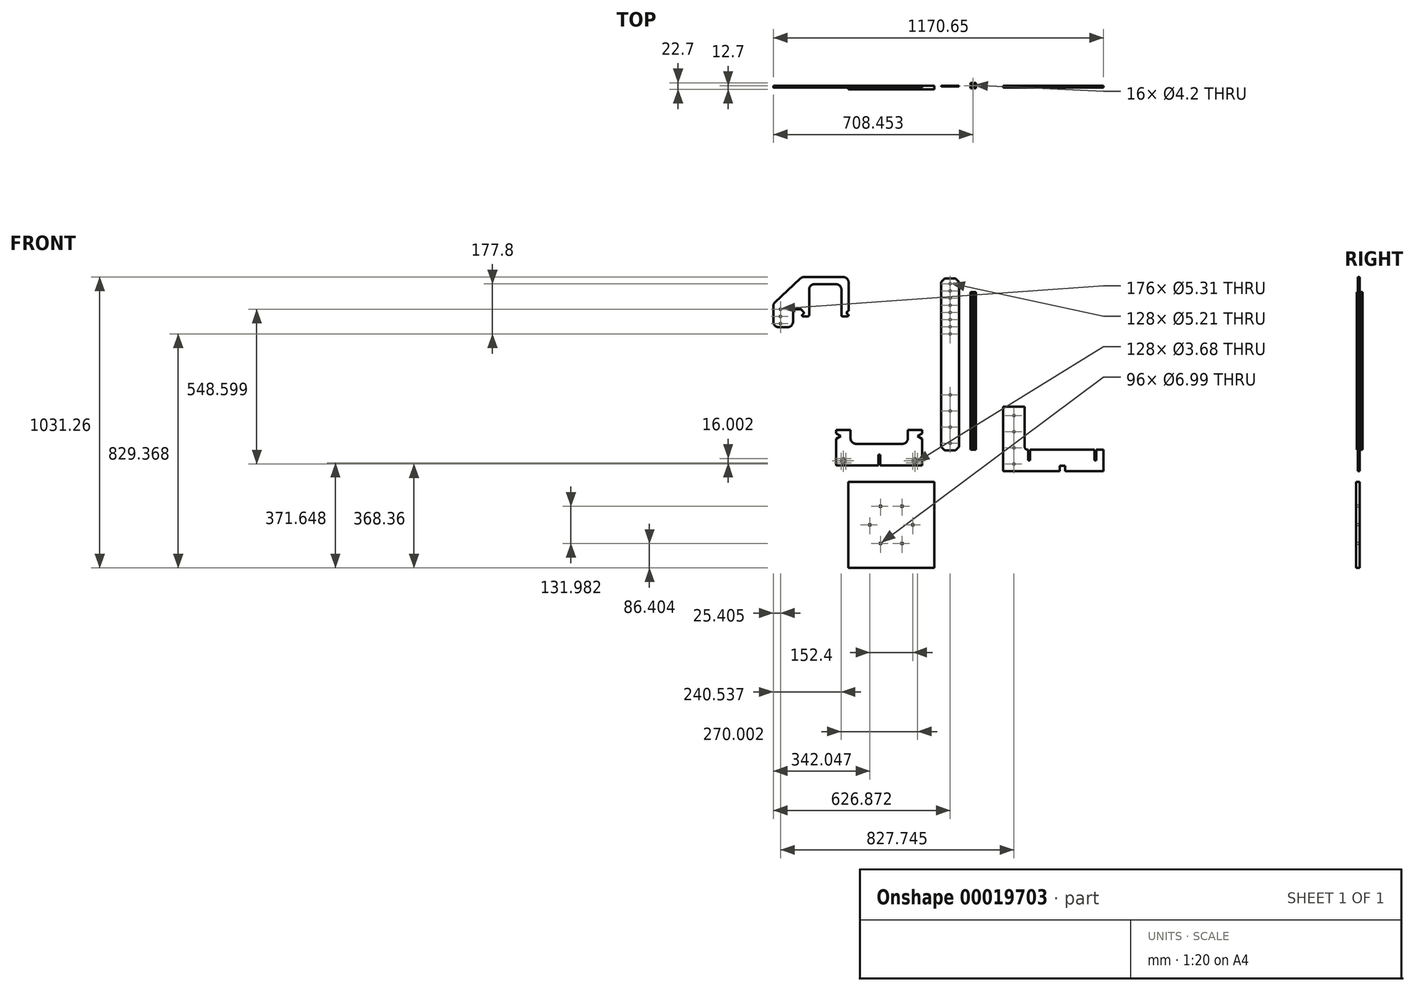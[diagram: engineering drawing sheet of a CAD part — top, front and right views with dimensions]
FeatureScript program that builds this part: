
annotation { "Feature Type Name" : "Feature", "Feature Type Description" : "" }
export const myFeature = defineFeature(function(context is Context, id is Id, definition is map)
    precondition{}
    {
        {
            var Q0;
            Q0=qCreatedBy(makeId("Front.planeOp"),FACE);
            var sketch = newSketch(context, id + "F0", { "sketchPlane" : qUnion([Q0])});
            skLineSegment(sketch, "E0.bottom", {"start": v(76.2, 0) * mm, "end": v(88.9, 0) * mm});
            skLineSegment(sketch, "E0.top", {"start": v(0, -76.2) * mm, "end": v(355.6, -76.2) * mm});
            skLineSegment(sketch, "E0.left", {"start": v(0, 0) * mm, "end": v(0, -76.2) * mm});
            skLineSegment(sketch, "E0.right", {"start": v(355.6, 0) * mm, "end": v(355.6, -76.2) * mm});
            skLineSegment(sketch, "E1.top", {"start": v(0, 152.4) * mm, "end": v(76.2, 152.4) * mm});
            skLineSegment(sketch, "E1.left", {"start": v(0, 0) * mm, "end": v(0, 152.4) * mm});
            skLineSegment(sketch, "E1.right", {"start": v(76.2, 0) * mm, "end": v(76.2, 152.4) * mm});
            skLineSegment(sketch, "E2.top", {"start": v(88.9, -38.1) * mm, "end": v(95.25, -38.1) * mm});
            skLineSegment(sketch, "E2.left", {"start": v(88.9, 0) * mm, "end": v(88.9, -38.1) * mm});
            skLineSegment(sketch, "E2.right", {"start": v(95.25, 0) * mm, "end": v(95.25, -38.1) * mm});
            skLineSegment(sketch, "E3.top", {"start": v(323.85, -38.1) * mm, "end": v(330.2, -38.1) * mm});
            skLineSegment(sketch, "E3.left", {"start": v(323.85, 0) * mm, "end": v(323.85, -38.1) * mm});
            skLineSegment(sketch, "E3.right", {"start": v(330.2, 0) * mm, "end": v(330.2, -38.1) * mm});
            skLineSegment(sketch, "E4.trimOffspring", {"start": v(95.25, 0) * mm, "end": v(323.85, 0) * mm});
            skLineSegment(sketch, "E5.trimOffspring", {"start": v(330.2, 0) * mm, "end": v(355.6, 0) * mm});
            skSolve(sketch);
        }
        {
            var Q0;
            Q0 = qSketchRegion(id + "F0", true);
            extrude(context, id + "F1", {"entities" : qUnion([Q0]), "depth" : 6.35 * mm});
        }
        {
            var Q0;
            Q0=qCreatedBy(makeId("Front.planeOp"),FACE);
            var sketch = newSketch(context, id + "F2", { "sketchPlane" : qUnion([Q0])});
            skLineSegment(sketch, "E6.bottom", {"start": v(-541.11, 20.69) * mm, "end": v(-337.91, 20.69) * mm});
            skLineSegment(sketch, "E6.top", {"start": v(-591.91, -55.51) * mm, "end": v(-442.69, -55.51) * mm});
            skLineSegment(sketch, "E6.left", {"start": v(-591.91, 20.69) * mm, "end": v(-591.91, -55.51) * mm});
            skLineSegment(sketch, "E6.right", {"start": v(-287.11, 20.69) * mm, "end": v(-287.11, -55.51) * mm});
            skLineSegment(sketch, "E7.top", {"start": v(-591.91, 70.22) * mm, "end": v(-541.11, 70.22) * mm});
            skLineSegment(sketch, "E7.left", {"start": v(-591.91, 20.69) * mm, "end": v(-591.91, 38.47) * mm});
            skLineSegment(sketch, "E7.right", {"start": v(-541.11, 20.69) * mm, "end": v(-541.11, 70.22) * mm});
            skLineSegment(sketch, "E8.top", {"start": v(-287.11, 70.22) * mm, "end": v(-337.91, 70.22) * mm});
            skLineSegment(sketch, "E8.left", {"start": v(-287.11, 20.69) * mm, "end": v(-287.11, 38.47) * mm});
            skLineSegment(sketch, "E8.right", {"start": v(-337.91, 20.69) * mm, "end": v(-337.91, 70.22) * mm});
            skLineSegment(sketch, "E9.top", {"start": v(-442.69, -17.41) * mm, "end": v(-436.34, -17.41) * mm});
            skLineSegment(sketch, "E9.left", {"start": v(-442.69, -55.51) * mm, "end": v(-442.69, -17.41) * mm});
            skLineSegment(sketch, "E9.right", {"start": v(-436.34, -55.51) * mm, "end": v(-436.34, -17.41) * mm});
            skLineSegment(sketch, "E10.trimOffspring", {"start": v(-318.86, -55.51) * mm, "end": v(-287.11, -55.51) * mm});
            skLineSegment(sketch, "E11.trimOffspring", {"start": v(-436.34, -55.51) * mm, "end": v(-325.21, -55.51) * mm});
            skLineSegment(sketch, "E12", {"start": v(-325.21, -55.51) * mm, "end": v(-318.86, -55.51) * mm});
            skLineSegment(sketch, "E13", {"start": v(-591.91, 57.52) * mm, "end": v(-575.41, 48) * mm});
            skLineSegment(sketch, "E14", {"start": v(-575.41, 48) * mm, "end": v(-591.91, 38.47) * mm});
            skLineSegment(sketch, "E15", {"start": v(-439.51, 20.69) * mm, "end": v(-439.51, -17.41) * mm, "construction": true});
            skLineSegment(sketch, "E16.MirrorCS", {"start": v(-287.11, 57.52) * mm, "end": v(-303.6, 48) * mm});
            skLineSegment(sketch, "E17.MirrorCS", {"start": v(-303.6, 48) * mm, "end": v(-287.11, 38.47) * mm});
            skLineSegment(sketch, "E18.trimOffspring", {"start": v(-591.91, 57.52) * mm, "end": v(-591.91, 70.22) * mm});
            skLineSegment(sketch, "E19.trimOffspring", {"start": v(-287.11, 57.52) * mm, "end": v(-287.11, 70.22) * mm});
            skSolve(sketch);
        }
        {
            var Q0;
            Q0 = qSketchRegion(id + "F2", true);
            extrude(context, id + "F3", {"entities" : qUnion([Q0]), "depth" : 6.35 * mm});
        }
        {
            var Q0;
            Q0=qCreatedBy(makeId("Front.planeOp"),FACE);
            var sketch = newSketch(context, id + "F4", { "sketchPlane" : qUnion([Q0])});
            skLineSegment(sketch, "E20.bottom", {"start": v(-815.05, 516.85) * mm, "end": v(-750.47, 516.85) * mm, "construction": true});
            skLineSegment(sketch, "E21.bottom", {"start": v(-713.45, 472.4) * mm, "end": v(-688.05, 472.4) * mm});
            skLineSegment(sketch, "E21.top", {"start": v(-713.45, 612.1) * mm, "end": v(-548.35, 612.1) * mm});
            skLineSegment(sketch, "E22.top", {"start": v(-688.05, 586.7) * mm, "end": v(-573.75, 586.7) * mm});
            skLineSegment(sketch, "E22.left", {"start": v(-688.05, 472.4) * mm, "end": v(-688.05, 586.7) * mm});
            skLineSegment(sketch, "E22.right", {"start": v(-573.75, 472.4) * mm, "end": v(-573.75, 586.7) * mm});
            skLineSegment(sketch, "E23.trimOffspring", {"start": v(-573.75, 472.4) * mm, "end": v(-548.35, 472.4) * mm});
            skArc(sketch, "E24", {"start": v(-713.45, 478.75) * mm, "mid": v(-707.1, 485.1) * mm, "end": v(-713.45, 491.45) * mm});
            skLineSegment(sketch, "E25.trimOffspring", {"start": v(-548.35, 574) * mm, "end": v(-548.35, 612.1) * mm});
            skLineSegment(sketch, "E26", {"start": v(-815.05, 516.85) * mm, "end": v(-815.05, 497.8) * mm});
            skCircle(sketch, "E27", {"center": v(-789.65, 497.8) * mm, "radius": 2.65 * mm});
            skCircle(sketch, "E28.0.1.0", {"center": v(-789.65, 472.4) * mm, "radius": 2.65 * mm});
            skCircle(sketch, "E28.0.2.0", {"center": v(-789.65, 447) * mm, "radius": 2.65 * mm});
            skLineSegment(sketch, "E29", {"start": v(-548.35, 574) * mm, "end": v(-548.35, 491.45) * mm});
            skLineSegment(sketch, "E30", {"start": v(-745.2, 497.8) * mm, "end": v(-713.45, 497.8) * mm});
            skLineSegment(sketch, "E31", {"start": v(-713.45, 497.8) * mm, "end": v(-713.45, 491.45) * mm});
            skPoint(sketch, "E32.orphan", {"position": v(-745.2, 472.4) * mm});
            skLineSegment(sketch, "E33", {"start": v(-750.47, 516.85) * mm, "end": v(-713.45, 516.85) * mm, "construction": true});
            skLineSegment(sketch, "E34", {"start": v(-713.45, 516.85) * mm, "end": v(-713.45, 612.1) * mm, "construction": true});
            skPoint(sketch, "E35.trimOffspring.end.orphan", {"position": v(-734.5, 612.1) * mm});
            skArc(sketch, "E36.1.0.0", {"start": v(-548.35, 491.45) * mm, "mid": v(-554.7, 485.1) * mm, "end": v(-548.35, 478.75) * mm});
            skLineSegment(sketch, "E36.direction1", {"start": v(-713.45, 485.1) * mm, "end": v(-548.35, 485.1) * mm, "construction": true});
            skLineSegment(sketch, "E37.trimOffspring", {"start": v(-713.45, 478.75) * mm, "end": v(-713.45, 472.4) * mm});
            skLineSegment(sketch, "E38.trimOffspring", {"start": v(-548.35, 478.75) * mm, "end": v(-548.35, 472.4) * mm});
            skLineSegment(sketch, "E39", {"start": v(-745.2, 497.8) * mm, "end": v(-745.2, 434.3) * mm});
            skLineSegment(sketch, "E40", {"start": v(-745.2, 434.3) * mm, "end": v(-815.05, 434.3) * mm});
            skLineSegment(sketch, "E41", {"start": v(-815.05, 434.3) * mm, "end": v(-815.05, 497.8) * mm});
            skLineSegment(sketch, "E42", {"start": v(-815.05, 516.85) * mm, "end": v(-713.45, 612.1) * mm});
            skSolve(sketch);
        }
        {
            var Q0;
            Q0 = qSketchRegion(id + "F4", true);
            extrude(context, id + "F5", {"entities" : qUnion([Q0]), "depth" : 6.35 * mm});
        }
        {
            var Q0;
            Q0=qCreatedBy(makeId("Front.planeOp"),FACE);
            var sketch = newSketch(context, id + "F6", { "sketchPlane" : qUnion([Q0])});
            skLineSegment(sketch, "E43.bottom", {"start": v(-549.2, -114.36) * mm, "end": v(-244.4, -114.36) * mm});
            skLineSegment(sketch, "E43.top", {"start": v(-549.2, -419.16) * mm, "end": v(-244.4, -419.16) * mm});
            skLineSegment(sketch, "E43.left", {"start": v(-549.2, -114.36) * mm, "end": v(-549.2, -419.16) * mm});
            skLineSegment(sketch, "E43.right", {"start": v(-244.4, -114.36) * mm, "end": v(-244.4, -419.16) * mm});
            skSolve(sketch);
        }
        {
            var Q0;
            Q0 = qSketchRegion(id + "F6", true);
            extrude(context, id + "F7", {"entities" : qUnion([Q0]), "depth" : 12.7 * mm});
        }
        {
            var Q0;
            Q0=makeQuery(id+"F1.opExtrude","CAP_FACE",FACE,{"disambiguationData":[OSD([sQuery(id+"F0.wireOp",EDGE,"E0.bottom"),sQuery(id+"F0.wireOp",EDGE,"E0.top"),sQuery(id+"F0.wireOp",EDGE,"E0.left"),sQuery(id+"F0.wireOp",EDGE,"E0.right"),sQuery(id+"F0.wireOp",EDGE,"E1.top"),sQuery(id+"F0.wireOp",EDGE,"E1.left"),sQuery(id+"F0.wireOp",EDGE,"E1.right"),sQuery(id+"F0.wireOp",EDGE,"a85b3c0d-053f-45aa-b62b-9afe83705e7b.bottom"),sQuery(id+"F0.wireOp",EDGE,"a85b3c0d-053f-45aa-b62b-9afe83705e7b.top"),sQuery(id+"F0.wireOp",EDGE,"a85b3c0d-053f-45aa-b62b-9afe83705e7b.right"),sQuery(id+"F0.wireOp",EDGE,"E2.top"),sQuery(id+"F0.wireOp",EDGE,"E2.left"),sQuery(id+"F0.wireOp",EDGE,"E2.right"),sQuery(id+"F0.wireOp",EDGE,"E3.top"),sQuery(id+"F0.wireOp",EDGE,"E3.left"),sQuery(id+"F0.wireOp",EDGE,"E3.right"),sQuery(id+"F0.wireOp",EDGE,"2a624cb3-e000-4eb9-9106-63d80287ee97.trimOffspring"),sQuery(id+"F0.wireOp",EDGE,"E4.trimOffspring"),sQuery(id+"F0.wireOp",EDGE,"E5.trimOffspring")])],"isStart":false});
            var sketch = newSketch(context, id + "F8", { "sketchPlane" : qUnion([Q0])});
            skCircle(sketch, "E44", {"center": v(38.1, -50.8) * mm, "radius": 2.65 * mm});
            skCircle(sketch, "E45.0.1.0", {"center": v(38.1, 6.35) * mm, "radius": 2.65 * mm});
            skCircle(sketch, "E45.0.2.0", {"center": v(38.1, 63.5) * mm, "radius": 2.65 * mm});
            skCircle(sketch, "E46", {"center": v(38.1, 120.65) * mm, "radius": 2.65 * mm});
            skSolve(sketch);
        }
        {
            var Q0;
            Q0 = qSketchRegion(id + "F8", true);
            extrude(context, id + "F9", {"entities" : qUnion([Q0]), "operationType" : NewBodyOperationType.REMOVE, "endBound" : BoundingType.SYMMETRIC, "oppositeDirection" : true, "depth" : 25.4 * mm});
        }
        {
            var Q0;
            Q0=makeQuery(id+"F7.opExtrude","CAP_FACE",FACE,{"disambiguationData":[OSD([sQuery(id+"F6.wireOp",EDGE,"E43.bottom"),sQuery(id+"F6.wireOp",EDGE,"E43.top"),sQuery(id+"F6.wireOp",EDGE,"E43.left"),sQuery(id+"F6.wireOp",EDGE,"E43.right")])],"isStart":false});
            var sketch = newSketch(context, id + "F10", { "sketchPlane" : qUnion([Q0])});
            skCircle(sketch, "E47", {"center": v(-396.8, -266.76) * mm, "radius": 76.2 * mm, "construction": true});
            skCircle(sketch, "E48", {"center": v(-473, -266.76) * mm, "radius": 3.5 * mm});
            skCircle(sketch, "E49", {"center": v(-320.6, -266.76) * mm, "radius": 3.5 * mm});
            skCircle(sketch, "E50", {"center": v(-434.9, -200.77) * mm, "radius": 3.5 * mm});
            skCircle(sketch, "E51", {"center": v(-358.7, -200.77) * mm, "radius": 3.5 * mm});
            skCircle(sketch, "E52", {"center": v(-434.9, -332.76) * mm, "radius": 3.5 * mm});
            skCircle(sketch, "E53", {"center": v(-358.7, -332.76) * mm, "radius": 3.5 * mm});
            skLineSegment(sketch, "E54", {"start": v(-473, -266.76) * mm, "end": v(-434.9, -200.77) * mm, "construction": true});
            skLineSegment(sketch, "E55", {"start": v(-434.9, -200.77) * mm, "end": v(-358.7, -200.77) * mm, "construction": true});
            skLineSegment(sketch, "E56", {"start": v(-358.7, -200.77) * mm, "end": v(-320.6, -266.76) * mm, "construction": true});
            skLineSegment(sketch, "E57", {"start": v(-320.6, -266.76) * mm, "end": v(-358.7, -332.76) * mm, "construction": true});
            skLineSegment(sketch, "E58", {"start": v(-358.7, -332.76) * mm, "end": v(-434.9, -332.76) * mm, "construction": true});
            skLineSegment(sketch, "E59", {"start": v(-434.9, -332.76) * mm, "end": v(-473, -266.76) * mm, "construction": true});
            skSolve(sketch);
        }
        {
            var Q0;
            Q0 = qSketchRegion(id + "F10", true);
            extrude(context, id + "F11", {"entities" : qUnion([Q0]), "operationType" : NewBodyOperationType.REMOVE, "oppositeDirection" : true, "depth" : 25.4 * mm});
        }
        {
            var Q0;
            Q0=makeQuery(id+"F3.opExtrude","CAP_FACE",FACE,{"disambiguationData":[OSD([sQuery(id+"F2.wireOp",EDGE,"E6.bottom"),sQuery(id+"F2.wireOp",EDGE,"E6.top"),sQuery(id+"F2.wireOp",EDGE,"E6.left"),sQuery(id+"F2.wireOp",EDGE,"E6.right"),sQuery(id+"F2.wireOp",EDGE,"E7.top"),sQuery(id+"F2.wireOp",EDGE,"E7.left"),sQuery(id+"F2.wireOp",EDGE,"E7.right"),sQuery(id+"F2.wireOp",EDGE,"E8.top"),sQuery(id+"F2.wireOp",EDGE,"E8.left"),sQuery(id+"F2.wireOp",EDGE,"E8.right"),sQuery(id+"F2.wireOp",EDGE,"E9.top"),sQuery(id+"F2.wireOp",EDGE,"E9.left"),sQuery(id+"F2.wireOp",EDGE,"E9.right"),sQuery(id+"F2.wireOp",EDGE,"E10.trimOffspring"),sQuery(id+"F2.wireOp",EDGE,"E11.trimOffspring"),sQuery(id+"F2.wireOp",EDGE,"E12"),sQuery(id+"F2.wireOp",EDGE,"E13"),sQuery(id+"F2.wireOp",EDGE,"E14"),sQuery(id+"F2.wireOp",EDGE,"E16.MirrorCS"),sQuery(id+"F2.wireOp",EDGE,"E17.MirrorCS"),sQuery(id+"F2.wireOp",EDGE,"E18.trimOffspring"),sQuery(id+"F2.wireOp",EDGE,"E19.trimOffspring")])],"isStart":false});
            var sketch = newSketch(context, id + "F12", { "sketchPlane" : qUnion([Q0])});
            skCircle(sketch, "E60", {"center": v(-566.51, -39.51) * mm, "radius": 8 * mm, "construction": true});
            skLineSegment(sketch, "E61", {"start": v(-566.51, -31.5) * mm, "end": v(-566.51, -47.51) * mm, "construction": true});
            skLineSegment(sketch, "E62", {"start": v(-574.51, -39.51) * mm, "end": v(-558.51, -39.51) * mm, "construction": true});
            skCircle(sketch, "E63", {"center": v(-566.51, -31.5) * mm, "radius": 1.84 * mm});
            skCircle(sketch, "E64", {"center": v(-558.51, -39.51) * mm, "radius": 1.84 * mm});
            skCircle(sketch, "E65", {"center": v(-566.51, -47.51) * mm, "radius": 1.84 * mm});
            skCircle(sketch, "E66", {"center": v(-574.51, -39.51) * mm, "radius": 1.84 * mm});
            skLineSegment(sketch, "E67", {"start": v(-439.51, -17.41) * mm, "end": v(-439.51, -47.51) * mm, "construction": true});
            skCircle(sketch, "E68.MirrorC", {"center": v(-304.51, -39.51) * mm, "radius": 1.84 * mm});
            skCircle(sketch, "E69.MirrorC", {"center": v(-312.51, -31.5) * mm, "radius": 1.84 * mm});
            skCircle(sketch, "E70.MirrorC", {"center": v(-320.51, -39.51) * mm, "radius": 1.84 * mm});
            skCircle(sketch, "E71.MirrorC", {"center": v(-312.51, -47.51) * mm, "radius": 1.84 * mm});
            skLineSegment(sketch, "E72.MirrorCS", {"start": v(-312.51, -31.5) * mm, "end": v(-312.51, -47.51) * mm, "construction": true});
            skCircle(sketch, "E73.MirrorC", {"center": v(-312.51, -39.51) * mm, "radius": 8 * mm, "construction": true});
            skLineSegment(sketch, "E74.MirrorCS", {"start": v(-304.51, -39.51) * mm, "end": v(-320.51, -39.51) * mm, "construction": true});
            skLineSegment(sketch, "E75", {"start": v(-566.51, -39.51) * mm, "end": v(-439.51, -39.51) * mm, "construction": true});
            skLineSegment(sketch, "E76", {"start": v(-439.51, -39.51) * mm, "end": v(-312.51, -39.51) * mm, "construction": true});
            skSolve(sketch);
        }
        {
            var Q0;
            Q0 = qSketchRegion(id + "F12", true);
            extrude(context, id + "F13", {"entities" : qUnion([Q0]), "operationType" : NewBodyOperationType.REMOVE, "oppositeDirection" : true, "depth" : 25.4 * mm});
        }
        {
            var Q0;
            Q0=makeQuery(id+"F1.opExtrude","CAP_FACE",FACE,{"disambiguationData":[OSD([sQuery(id+"F0.wireOp",EDGE,"E0.bottom"),sQuery(id+"F0.wireOp",EDGE,"E0.top"),sQuery(id+"F0.wireOp",EDGE,"E0.left"),sQuery(id+"F0.wireOp",EDGE,"E0.right"),sQuery(id+"F0.wireOp",EDGE,"E1.top"),sQuery(id+"F0.wireOp",EDGE,"E1.left"),sQuery(id+"F0.wireOp",EDGE,"E1.right"),sQuery(id+"F0.wireOp",EDGE,"a85b3c0d-053f-45aa-b62b-9afe83705e7b.bottom"),sQuery(id+"F0.wireOp",EDGE,"a85b3c0d-053f-45aa-b62b-9afe83705e7b.top"),sQuery(id+"F0.wireOp",EDGE,"a85b3c0d-053f-45aa-b62b-9afe83705e7b.right"),sQuery(id+"F0.wireOp",EDGE,"E2.top"),sQuery(id+"F0.wireOp",EDGE,"E2.left"),sQuery(id+"F0.wireOp",EDGE,"E2.right"),sQuery(id+"F0.wireOp",EDGE,"E3.top"),sQuery(id+"F0.wireOp",EDGE,"E3.left"),sQuery(id+"F0.wireOp",EDGE,"E3.right"),sQuery(id+"F0.wireOp",EDGE,"2a624cb3-e000-4eb9-9106-63d80287ee97.trimOffspring"),sQuery(id+"F0.wireOp",EDGE,"E4.trimOffspring"),sQuery(id+"F0.wireOp",EDGE,"E5.trimOffspring")])],"isStart":false});
            var sketch = newSketch(context, id + "F14", { "sketchPlane" : qUnion([Q0])});
            skLineSegment(sketch, "E77.bottom", {"start": v(200.03, -76.2) * mm, "end": v(219.08, -76.2) * mm});
            skLineSegment(sketch, "E77.top", {"start": v(200.03, -57.15) * mm, "end": v(219.08, -57.15) * mm});
            skLineSegment(sketch, "E77.left", {"start": v(200.03, -76.2) * mm, "end": v(200.03, -57.15) * mm});
            skLineSegment(sketch, "E77.right", {"start": v(219.08, -76.2) * mm, "end": v(219.08, -57.15) * mm});
            skPoint(sketch, "E78", {"position": v(209.55, -57.15) * mm});
            skLineSegment(sketch, "E79", {"start": v(92.08, -38.1) * mm, "end": v(209.55, -57.15) * mm, "construction": true});
            skLineSegment(sketch, "E80", {"start": v(327.03, -38.1) * mm, "end": v(209.55, -57.15) * mm, "construction": true});
            skSolve(sketch);
        }
        {
            var Q0;
            Q0 = qSketchRegion(id + "F14", true);
            extrude(context, id + "F15", {"entities" : qUnion([Q0]), "operationType" : NewBodyOperationType.REMOVE, "endBound" : BoundingType.THROUGH_ALL, "oppositeDirection" : true, "depth" : 25.4 * mm});
        }
        {
            var Q0;
            Q0=makeQuery(id+"F3.opExtrude","SWEPT_EDGE",EDGE,{"disambiguationData":[OSD([sQuery(id+"F2.wireOp",EDGE,"E6.bottom"),sQuery(id+"F2.wireOp",EDGE,"E7.right")])]});
            var Q1;
            Q1=makeQuery(id+"F3.opExtrude","SWEPT_EDGE",EDGE,{"disambiguationData":[OSD([sQuery(id+"F2.wireOp",EDGE,"E6.bottom"),sQuery(id+"F2.wireOp",EDGE,"E8.right")])]});
            var Q2;
            Q2=makeQuery(id+"F5.opExtrude","SWEPT_EDGE",EDGE,{"disambiguationData":[OSD([sQuery(id+"F4.wireOp",EDGE,"E22.top"),sQuery(id+"F4.wireOp",EDGE,"E22.right")])]});
            var Q3;
            Q3=makeQuery(id+"F5.opExtrude","SWEPT_EDGE",EDGE,{"disambiguationData":[OSD([sQuery(id+"F4.wireOp",EDGE,"E22.top"),sQuery(id+"F4.wireOp",EDGE,"E22.left")])]});
            var Q4;
            Q4=makeQuery(id+"F5.opExtrude","SWEPT_EDGE",EDGE,{"disambiguationData":[OSD([sQuery(id+"F4.wireOp",EDGE,"E20.bottom"),sQuery(id+"F4.wireOp",EDGE,"E35.trimOffspring")])]});
            var Q5;
            Q5=makeQuery(id+"F5.opExtrude","SWEPT_EDGE",EDGE,{"disambiguationData":[OSD([sQuery(id+"F4.wireOp",EDGE,"E20.top"),sQuery(id+"F4.wireOp",EDGE,"E21.left")])]});
            var Q6;
            Q6=makeQuery(id+"F5.opExtrude","SWEPT_EDGE",EDGE,{"disambiguationData":[OSD([sQuery(id+"F4.wireOp",EDGE,"E21.top"),sQuery(id+"F4.wireOp",EDGE,"E34")])]});
            var Q7;
            Q7=makeQuery(id+"F5.opExtrude","SWEPT_EDGE",EDGE,{"disambiguationData":[OSD([sQuery(id+"F4.wireOp",EDGE,"E21.top"),sQuery(id+"F4.wireOp",EDGE,"E25.trimOffspring")])]});
            var Q8;
            Q8=makeQuery(id+"F5.opExtrude","SWEPT_EDGE",EDGE,{"disambiguationData":[OSD([sQuery(id+"F4.wireOp",EDGE,"E26"),sQuery(id+"F4.wireOp",EDGE,"E42")])]});
            var Q9;
            Q9=makeQuery(id+"F5.opExtrude","SWEPT_EDGE",EDGE,{"disambiguationData":[OSD([sQuery(id+"F4.wireOp",EDGE,"E40"),sQuery(id+"F4.wireOp",EDGE,"E41")])]});
            var Q10;
            Q10=makeQuery(id+"F5.opExtrude","SWEPT_EDGE",EDGE,{"disambiguationData":[OSD([sQuery(id+"F4.wireOp",EDGE,"E39"),sQuery(id+"F4.wireOp",EDGE,"E40")])]});
            fillet(context, id + "F16", {"entities" : qUnion([Q0, Q1, Q2, Q3, Q4, Q5, Q6, Q7, Q8, Q9, Q10]), "radius" : 19.05 * mm, "tangentPropagation" : true, "allowEdgeOverflow" : false});
        }
        {
            var Q0;
            Q0=makeQuery(id+"F1.opExtrude","SWEPT_EDGE",EDGE,{"disambiguationData":[OSD([sQuery(id+"F0.wireOp",EDGE,"E0.bottom"),sQuery(id+"F0.wireOp",EDGE,"E1.right")])]});
            fillet(context, id + "F17", {"entities" : qUnion([Q0]), "radius" : 9.52 * mm, "tangentPropagation" : true, "allowEdgeOverflow" : false});
        }
        {
            var Q0;
            Q0=qCreatedBy(makeId("Top.planeOp"),FACE);
            var sketch = newSketch(context, id + "F18", { "sketchPlane" : qUnion([Q0])});
            skLineSegment(sketch, "E81.rect.bottom", {"start": v(-116.6, 10) * mm, "end": v(-96.6, 10) * mm});
            skLineSegment(sketch, "E81.rect.top", {"start": v(-116.6, -10) * mm, "end": v(-96.6, -10) * mm});
            skLineSegment(sketch, "E81.rect.left", {"start": v(-116.6, 10) * mm, "end": v(-116.6, -10) * mm});
            skLineSegment(sketch, "E81.rect.right", {"start": v(-96.6, 10) * mm, "end": v(-96.6, -10) * mm});
            skPoint(sketch, "E81.rect.middle", {"position": v(-106.6, 0) * mm});
            skLineSegment(sketch, "E82", {"start": v(-116.6, 10) * mm, "end": v(-96.6, -10) * mm, "construction": true});
            skLineSegment(sketch, "E83", {"start": v(-96.6, 10) * mm, "end": v(-116.6, -10) * mm, "construction": true});
            skSolve(sketch);
        }
        {
            var Q0;
            Q0 = qSketchRegion(id + "F18", true);
            extrude(context, id + "F19", {"entities" : qUnion([Q0]), "depth" : 558.8 * mm});
        }
        {
            var Q0;
            Q0=makeQuery(id+"F19.opExtrude","CAP_FACE",FACE,{"disambiguationData":[OSD([sQuery(id+"F18.wireOp",EDGE,"E81.rect.bottom"),sQuery(id+"F18.wireOp",EDGE,"E81.rect.top"),sQuery(id+"F18.wireOp",EDGE,"E81.rect.left"),sQuery(id+"F18.wireOp",EDGE,"E81.rect.right")])],"isStart":false});
            var sketch = newSketch(context, id + "F20", { "sketchPlane" : qUnion([Q0])});
            skLineSegment(sketch, "E84", {"start": v(-116.6, 10) * mm, "end": v(-96.6, -10) * mm, "construction": true});
            skLineSegment(sketch, "E85", {"start": v(-96.6, 10) * mm, "end": v(-116.6, -10) * mm, "construction": true});
            skLineSegment(sketch, "E86", {"start": v(-116.6, 10) * mm, "end": v(-109.6, 10) * mm, "construction": true});
            skLineSegment(sketch, "E87", {"start": v(-109.6, 10) * mm, "end": v(-103.6, 10) * mm});
            skLineSegment(sketch, "E88", {"start": v(-103.6, 10) * mm, "end": v(-96.6, 10) * mm, "construction": true});
            skLineSegment(sketch, "E89", {"start": v(-109.6, 10) * mm, "end": v(-109.6, 8) * mm});
            skLineSegment(sketch, "E90", {"start": v(-109.6, 8) * mm, "end": v(-112.6, 8) * mm});
            skLineSegment(sketch, "E91", {"start": v(-112.6, 8) * mm, "end": v(-108.6, 4) * mm});
            skLineSegment(sketch, "E92", {"start": v(-108.6, 4) * mm, "end": v(-104.6, 4) * mm});
            skLineSegment(sketch, "E93", {"start": v(-104.6, 4) * mm, "end": v(-100.6, 8) * mm});
            skLineSegment(sketch, "E94", {"start": v(-100.6, 8) * mm, "end": v(-103.6, 8) * mm});
            skLineSegment(sketch, "E95", {"start": v(-103.6, 8) * mm, "end": v(-103.6, 10) * mm});
            skLineSegment(sketch, "E96.1.0", {"start": v(-116.6, -10) * mm, "end": v(-116.6, -3) * mm, "construction": true});
            skLineSegment(sketch, "E96.1.1", {"start": v(-110.6, 2) * mm, "end": v(-114.6, 6) * mm});
            skLineSegment(sketch, "E96.1.2", {"start": v(-116.6, -3) * mm, "end": v(-114.6, -3) * mm});
            skLineSegment(sketch, "E96.1.3", {"start": v(-114.6, 6) * mm, "end": v(-114.6, 3) * mm});
            skLineSegment(sketch, "E96.1.4", {"start": v(-114.6, -3) * mm, "end": v(-114.6, -6) * mm});
            skLineSegment(sketch, "E96.1.5", {"start": v(-116.6, -3) * mm, "end": v(-116.6, 3) * mm});
            skLineSegment(sketch, "E96.1.6", {"start": v(-110.6, -2) * mm, "end": v(-110.6, 2) * mm});
            skLineSegment(sketch, "E96.1.7", {"start": v(-116.6, 3) * mm, "end": v(-116.6, 10) * mm, "construction": true});
            skLineSegment(sketch, "E96.1.8", {"start": v(-114.6, -6) * mm, "end": v(-110.6, -2) * mm});
            skLineSegment(sketch, "E96.1.9", {"start": v(-114.6, 3) * mm, "end": v(-116.6, 3) * mm});
            skLineSegment(sketch, "E96.2.0", {"start": v(-96.6, -10) * mm, "end": v(-103.6, -10) * mm, "construction": true});
            skLineSegment(sketch, "E96.2.1", {"start": v(-108.6, -4) * mm, "end": v(-112.6, -8) * mm});
            skLineSegment(sketch, "E96.2.2", {"start": v(-103.6, -10) * mm, "end": v(-103.6, -8) * mm});
            skLineSegment(sketch, "E96.2.3", {"start": v(-112.6, -8) * mm, "end": v(-109.6, -8) * mm});
            skLineSegment(sketch, "E96.2.4", {"start": v(-103.6, -8) * mm, "end": v(-100.6, -8) * mm});
            skLineSegment(sketch, "E96.2.5", {"start": v(-103.6, -10) * mm, "end": v(-109.6, -10) * mm});
            skLineSegment(sketch, "E96.2.6", {"start": v(-104.6, -4) * mm, "end": v(-108.6, -4) * mm});
            skLineSegment(sketch, "E96.2.7", {"start": v(-109.6, -10) * mm, "end": v(-116.6, -10) * mm, "construction": true});
            skLineSegment(sketch, "E96.2.8", {"start": v(-100.6, -8) * mm, "end": v(-104.6, -4) * mm});
            skLineSegment(sketch, "E96.2.9", {"start": v(-109.6, -8) * mm, "end": v(-109.6, -10) * mm});
            skLineSegment(sketch, "E96.3.0", {"start": v(-96.6, 10) * mm, "end": v(-96.6, 3) * mm, "construction": true});
            skLineSegment(sketch, "E96.3.1", {"start": v(-102.6, -2) * mm, "end": v(-98.6, -6) * mm});
            skLineSegment(sketch, "E96.3.2", {"start": v(-96.6, 3) * mm, "end": v(-98.6, 3) * mm});
            skLineSegment(sketch, "E96.3.3", {"start": v(-98.6, -6) * mm, "end": v(-98.6, -3) * mm});
            skLineSegment(sketch, "E96.3.4", {"start": v(-98.6, 3) * mm, "end": v(-98.6, 6) * mm});
            skLineSegment(sketch, "E96.3.5", {"start": v(-96.6, 3) * mm, "end": v(-96.6, -3) * mm});
            skLineSegment(sketch, "E96.3.6", {"start": v(-102.6, 2) * mm, "end": v(-102.6, -2) * mm});
            skLineSegment(sketch, "E96.3.7", {"start": v(-96.6, -3) * mm, "end": v(-96.6, -10) * mm, "construction": true});
            skLineSegment(sketch, "E96.3.8", {"start": v(-98.6, 6) * mm, "end": v(-102.6, 2) * mm});
            skLineSegment(sketch, "E96.3.9", {"start": v(-98.6, -3) * mm, "end": v(-96.6, -3) * mm});
            skPoint(sketch, "E96.center", {"position": v(-106.6, 0) * mm});
            skCircle(sketch, "E97", {"center": v(-106.6, 0) * mm, "radius": 2.1 * mm});
            skSolve(sketch);
        }
        {
            var Q0;
            Q0 = qSketchRegion(id + "F20", true);
            extrude(context, id + "F21", {"entities" : qUnion([Q0]), "operationType" : NewBodyOperationType.REMOVE, "endBound" : BoundingType.THROUGH_ALL, "oppositeDirection" : true, "depth" : 25.4 * mm});
        }
        {
            var Q0;
            Q0=makeQuery(id+"F5.opExtrude","SWEPT_EDGE",EDGE,{"disambiguationData":[OSD([sQuery(id+"F4.wireOp",EDGE,"E21.bottom"),sQuery(id+"F4.wireOp",EDGE,"E37.trimOffspring")])]});
            var Q1;
            Q1=makeQuery(id+"F5.opExtrude","SWEPT_EDGE",EDGE,{"disambiguationData":[OSD([sQuery(id+"F4.wireOp",EDGE,"E21.bottom"),sQuery(id+"F4.wireOp",EDGE,"E22.left")])]});
            var Q2;
            Q2=makeQuery(id+"F5.opExtrude","SWEPT_EDGE",EDGE,{"disambiguationData":[OSD([sQuery(id+"F4.wireOp",EDGE,"E23.trimOffspring"),sQuery(id+"F4.wireOp",EDGE,"E38.trimOffspring")])]});
            var Q3;
            Q3=makeQuery(id+"F5.opExtrude","SWEPT_EDGE",EDGE,{"disambiguationData":[OSD([sQuery(id+"F4.wireOp",EDGE,"E22.right"),sQuery(id+"F4.wireOp",EDGE,"E23.trimOffspring")])]});
            var Q4;
            Q4=makeQuery(id+"F5.opExtrude","SWEPT_EDGE",EDGE,{"disambiguationData":[OSD([sQuery(id+"F4.wireOp",EDGE,"E30"),sQuery(id+"F4.wireOp",EDGE,"E31")])]});
            var Q5;
            Q5=makeQuery(id+"F5.opExtrude","SWEPT_EDGE",EDGE,{"disambiguationData":[OSD([sQuery(id+"F4.wireOp",EDGE,"E30"),sQuery(id+"F4.wireOp",EDGE,"E39")])]});
            fillet(context, id + "F22", {"entities" : qUnion([Q0, Q1, Q2, Q3, Q4, Q5]), "radius" : 4.76 * mm, "tangentPropagation" : true, "allowEdgeOverflow" : false});
        }
        {
            var Q0;
            Q0=qCreatedBy(makeId("Front.planeOp"),FACE);
            var sketch = newSketch(context, id + "F23", { "sketchPlane" : qUnion([Q0])});
            skLineSegment(sketch, "E98.bottom", {"start": v(-219.93, -2.54) * mm, "end": v(-156.43, -2.54) * mm});
            skLineSegment(sketch, "E98.top", {"start": v(-219.93, 607.06) * mm, "end": v(-156.43, 607.06) * mm});
            skLineSegment(sketch, "E98.left", {"start": v(-219.93, -2.54) * mm, "end": v(-219.93, 607.06) * mm});
            skLineSegment(sketch, "E98.right", {"start": v(-156.43, -2.54) * mm, "end": v(-156.43, 607.06) * mm});
            skLineSegment(sketch, "E99", {"start": v(-188.18, 607.06) * mm, "end": v(-188.18, -2.54) * mm, "construction": true});
            skCircle(sketch, "E100", {"center": v(-188.18, 22.86) * mm, "radius": 2.65 * mm});
            skCircle(sketch, "E101", {"center": v(-188.18, 80) * mm, "radius": 2.65 * mm});
            skCircle(sketch, "E102", {"center": v(-188.18, 137.16) * mm, "radius": 2.65 * mm});
            skCircle(sketch, "E103", {"center": v(-188.18, 194.3) * mm, "radius": 2.65 * mm});
            skCircle(sketch, "E104", {"center": v(-188.18, 588) * mm, "radius": 2.6 * mm});
            skCircle(sketch, "E105.1.0.0", {"center": v(-188.18, 562.6) * mm, "radius": 2.6 * mm});
            skCircle(sketch, "E105.2.0.0", {"center": v(-188.18, 537.2) * mm, "radius": 2.6 * mm});
            skCircle(sketch, "E105.3.0.0", {"center": v(-188.18, 511.8) * mm, "radius": 2.6 * mm});
            skCircle(sketch, "E105.4.0.0", {"center": v(-188.18, 486.4) * mm, "radius": 2.6 * mm});
            skCircle(sketch, "E105.5.0.0", {"center": v(-188.18, 461) * mm, "radius": 2.6 * mm});
            skCircle(sketch, "E105.6.0.0", {"center": v(-188.18, 435.6) * mm, "radius": 2.6 * mm});
            skCircle(sketch, "E105.7.0.0", {"center": v(-188.18, 410.2) * mm, "radius": 2.6 * mm});
            skLineSegment(sketch, "E105.direction1", {"start": v(-188.18, 588) * mm, "end": v(-188.18, 562.6) * mm, "construction": true});
            skSolve(sketch);
        }
        {
            var Q0;
            Q0 = qSketchRegion(id + "F23", true);
            extrude(context, id + "F24", {"entities" : qUnion([Q0]), "depth" : 3.17 * mm});
        }
        {
            var Q0;
            Q0=makeQuery(id+"F24.opExtrude","SWEPT_EDGE",EDGE,{"disambiguationData":[OSD([sQuery(id+"F23.wireOp",EDGE,"E98.bottom"),sQuery(id+"F23.wireOp",EDGE,"E98.left")])]});
            var Q1;
            Q1=makeQuery(id+"F24.opExtrude","SWEPT_EDGE",EDGE,{"disambiguationData":[OSD([sQuery(id+"F23.wireOp",EDGE,"E98.bottom"),sQuery(id+"F23.wireOp",EDGE,"E98.right")])]});
            var Q2;
            Q2=makeQuery(id+"F24.opExtrude","SWEPT_EDGE",EDGE,{"disambiguationData":[OSD([sQuery(id+"F23.wireOp",EDGE,"E98.top"),sQuery(id+"F23.wireOp",EDGE,"E98.left")])]});
            var Q3;
            Q3=makeQuery(id+"F24.opExtrude","SWEPT_EDGE",EDGE,{"disambiguationData":[OSD([sQuery(id+"F23.wireOp",EDGE,"E98.top"),sQuery(id+"F23.wireOp",EDGE,"E98.right")])]});
            chamfer(context, id + "F25", {"entities" : qUnion([Q0, Q1, Q2, Q3]), "width" : 12.7 * mm, "tangentPropagation" : true});
        }
    });
